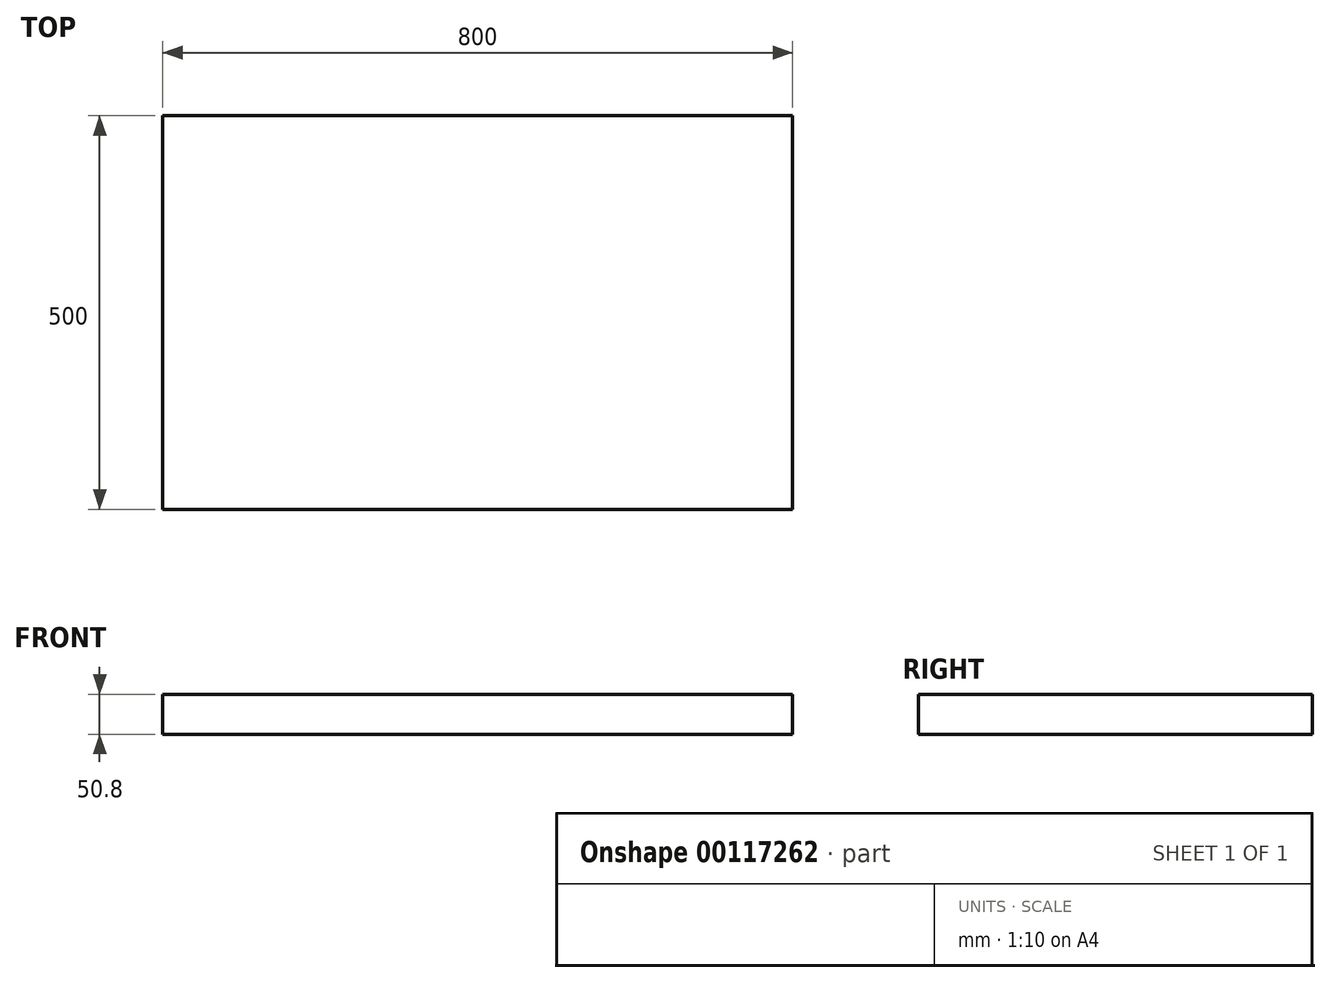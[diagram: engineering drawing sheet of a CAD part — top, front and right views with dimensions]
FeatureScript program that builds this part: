
annotation { "Feature Type Name" : "Feature", "Feature Type Description" : "" }
export const myFeature = defineFeature(function(context is Context, id is Id, definition is map)
    precondition{}
    {
        {
            var Q0;
            Q0=qCreatedBy(makeId("Top.planeOp"),FACE);
            var sketch = newSketch(context, id + "F0", { "sketchPlane" : qUnion([Q0])});
            skLineSegment(sketch, "E0.bottom", {"start": v(-379.66, 252.5) * mm, "end": v(420.34, 252.5) * mm});
            skLineSegment(sketch, "E0.top", {"start": v(-379.66, -247.5) * mm, "end": v(420.34, -247.5) * mm});
            skLineSegment(sketch, "E0.left", {"start": v(-379.66, 252.5) * mm, "end": v(-379.66, -247.5) * mm});
            skLineSegment(sketch, "E0.right", {"start": v(420.34, 252.5) * mm, "end": v(420.34, -247.5) * mm});
            skSolve(sketch);
        }
        {
            var Q0;
            Q0 = qSketchRegion(id + "F0", true);
            var Q1;
            Q1=makeQuery(id+"F0.imprint","IMPRINT",FACE,{"disambiguationData":[TD([[makeQuery(id+"F0.imprint","IMPRINT",EDGE,{"derivedFrom":sQuery(id+"F0.wireOp",EDGE,"E0.bottom")}),-1.0]])]});
            extrude(context, id + "F1", {"entities" : qUnion([Q0, Q1]), "depth" : 50.8 * mm, "offsetDistance" : 25 * mm});
        }
    });
